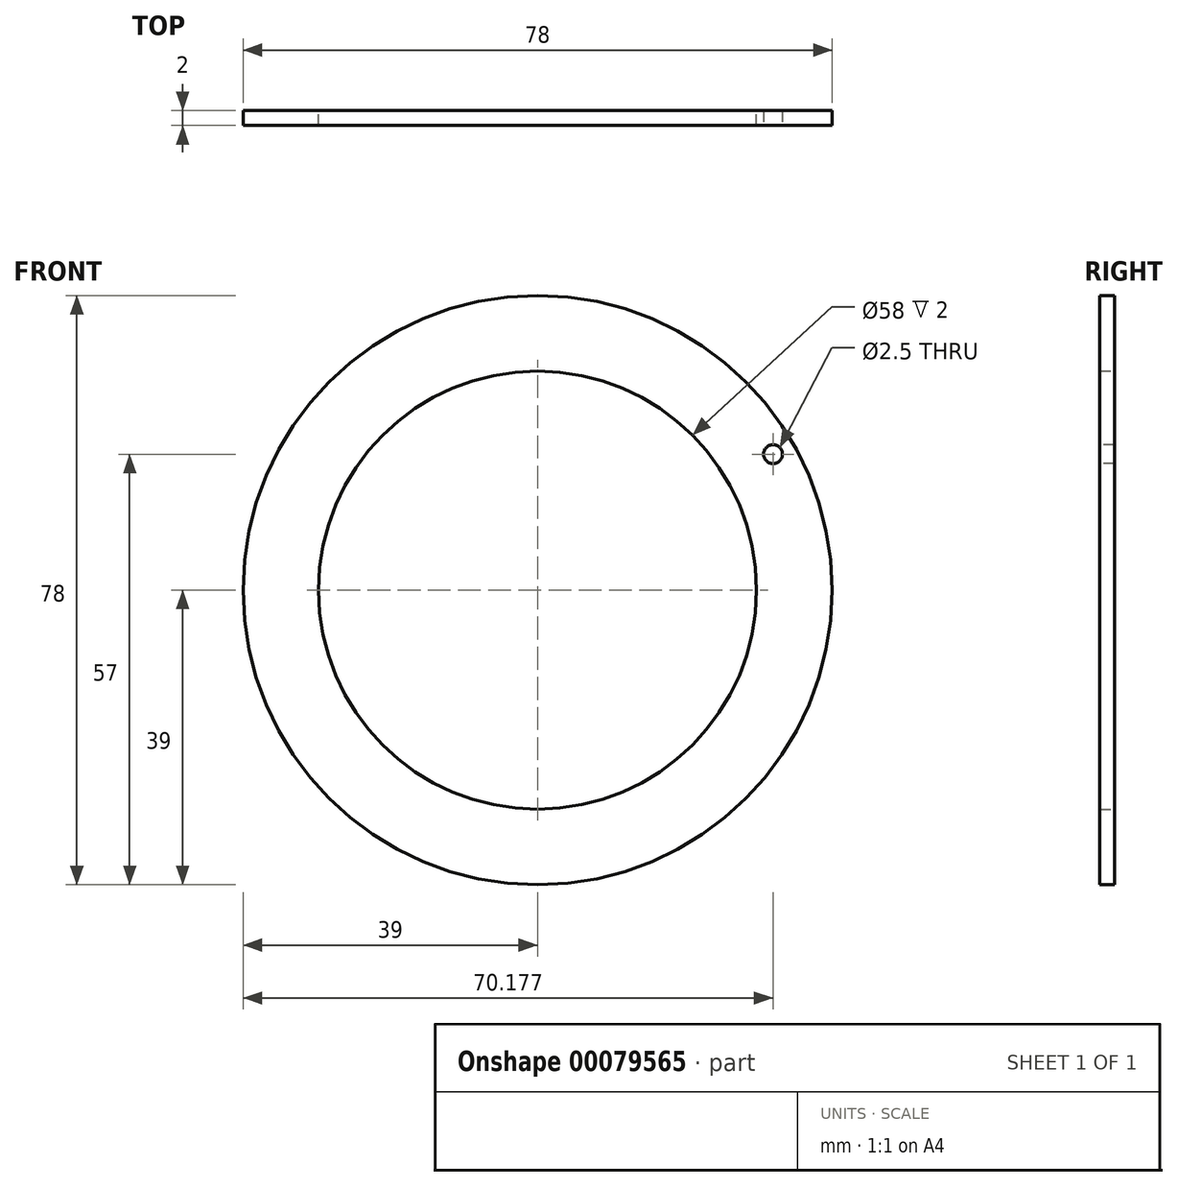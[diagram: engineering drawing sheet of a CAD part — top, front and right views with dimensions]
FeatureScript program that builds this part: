
annotation { "Feature Type Name" : "Feature", "Feature Type Description" : "" }
export const myFeature = defineFeature(function(context is Context, id is Id, definition is map)
    precondition{}
    {
        {
            var Q0;
            Q0=qCreatedBy(makeId("Front.planeOp"),FACE);
            var sketch = newSketch(context, id + "F0", { "sketchPlane" : qUnion([Q0])});
            skCircle(sketch, "E0", {"center": v(0, 0) * mm, "radius": 39 * mm});
            skCircle(sketch, "E1", {"center": v(0, 0) * mm, "radius": 29 * mm});
            skSolve(sketch);
        }
        {
            var Q0;
            Q0=makeQuery(id+"F0.imprint","IMPRINT",FACE,{"disambiguationData":[TD([[makeQuery(id+"F0.imprint","IMPRINT",EDGE,{"derivedFrom":sQuery(id+"F0.wireOp",EDGE,"E0")}),1.0]])]});
            extrude(context, id + "F1", {"entities" : qUnion([Q0]), "depth" : 2 * mm});
        }
        {
            var Q0;
            Q0=makeQuery(id+"F1.opExtrude","CAP_FACE",FACE,{"disambiguationData":[OSD([sQuery(id+"F0.wireOp",EDGE,"E0"),sQuery(id+"F0.wireOp",EDGE,"E1")])],"isStart":false});
            var sketch = newSketch(context, id + "F2", { "sketchPlane" : qUnion([Q0])});
            skCircle(sketch, "E2", {"center": v(0, 0) * mm, "radius": 36 * mm, "construction": true});
            skCircle(sketch, "E3", {"center": v(31.18, 18) * mm, "radius": 1.25 * mm});
            skLineSegment(sketch, "E4", {"start": v(0, 0) * mm, "end": v(31.18, 18) * mm, "construction": true});
            skSolve(sketch);
        }
        {
            var Q0;
            Q0=makeQuery(id+"F2.imprint","IMPRINT",FACE,{"disambiguationData":[TD([[makeQuery(id+"F2.imprint","IMPRINT",EDGE,{"derivedFrom":sQuery(id+"F2.wireOp",EDGE,"E3")}),1.0]])]});
            extrude(context, id + "F3", {"entities" : qUnion([Q0]), "operationType" : NewBodyOperationType.REMOVE, "endBound" : BoundingType.THROUGH_ALL, "oppositeDirection" : true, "depth" : 25 * mm});
        }
        {
            var Q0;
            Q0=qCreatedBy(makeId("Right.planeOp"),FACE);
            var sketch = newSketch(context, id + "F4", { "sketchPlane" : qUnion([Q0])});
            skLineSegment(sketch, "E5", {"start": v(-43.1, 0) * mm, "end": v(41.7, 0) * mm, "construction": true});
            skSolve(sketch);
        }
    });
